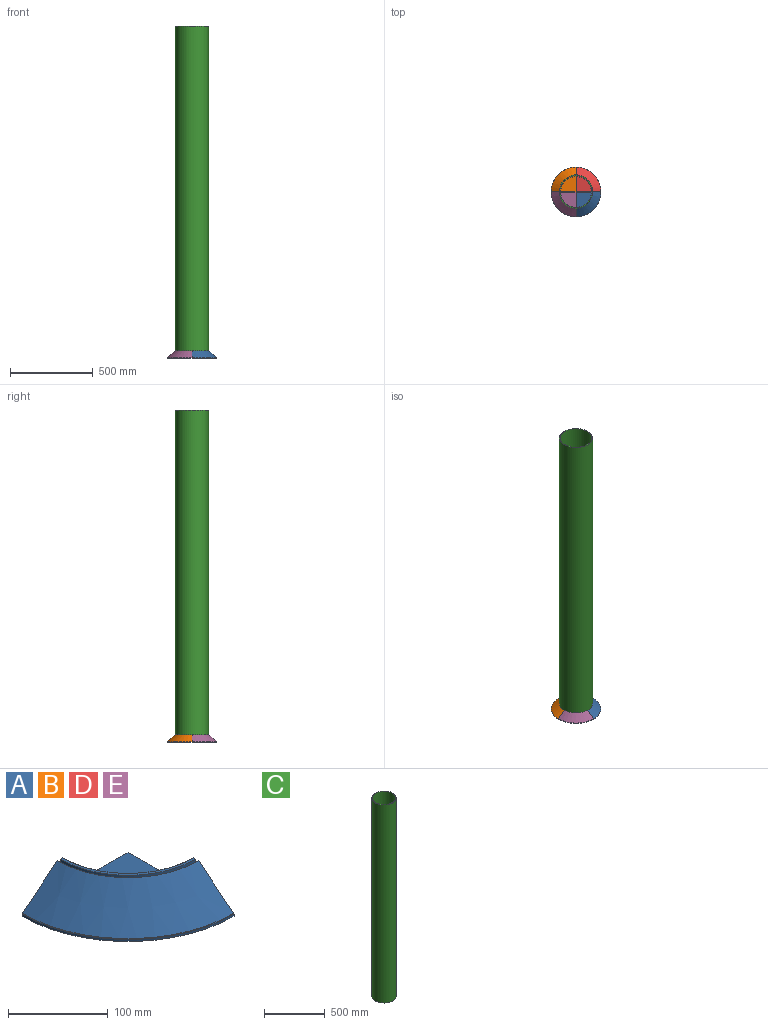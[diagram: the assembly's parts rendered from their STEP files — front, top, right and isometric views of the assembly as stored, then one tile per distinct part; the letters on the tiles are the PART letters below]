
ASSEMBLY  parts=5 mates=1
PART A: 13 faces, bbox 162.4x162.4x43 mm
  f0: plane 150x43mm, normal (1,0,0), area 1609.8mm2, adj f1,f2,f3,f4,f5,f6,f7,f8
  f1: plane 150x150mm, normal (0,0,-1), area 17671.5mm2, adj f0,f11,f12
  f2: plane 92x92mm, normal (0,0,1), area 6647.6mm2, adj f0,f6,f12
  f3: torus R=93mm, axis (0,0,1), area 227.9mm2, adj f0,f4,f6,f12
  f4: plane 96x96mm, normal (0,0,1), area 445.3mm2, adj f0,f3,f5,f12
  f5: cylinder r=96mm len=96mm, axis (0,0,-1), area 6031.9mm2, adj f0,f4,f7,f12
  f6: cylinder r=92mm len=92mm, axis (0,0,-1), area 5636mm2, adj f0,f2,f3,f12
  f7: plane 100x100mm, normal (0,0,1), area 615.8mm2, adj f0,f5,f10,f12
  f8: torus R=149mm, axis (0,0,1), area 210.9mm2, adj f0,f9,f11,f12
  f9: cone r=100mm half-angle=51.3deg, axis (0,0,-1), area 12459.4mm2, adj f0,f8,f10,f12
  f10: cylinder r=100mm len=100mm, axis (0,0,-1), area 6283.2mm2, adj f0,f7,f9,f12
  f11: cylinder r=150mm len=150mm, axis (0,0,1), area 593.6mm2, adj f0,f1,f8,f12
  f12: plane 150x43mm, normal (0,1,0), area 1609.8mm2, adj f0,f1,f2,f3,f4,f5,f6,f7
PART B: same geometry as A
PART C: 4 faces, bbox 200x200x2000 mm
  f0: cylinder r=96mm len=2000mm, axis (0,0,-1), area 1206371.6mm2, adj f2,f3
  f1: cylinder r=100mm len=2000mm, axis (0,0,-1), area 1256637.1mm2, adj f2,f3
  f2: plane 200x200mm, normal (0,0,1), area 2463mm2, adj f0,f1
  f3: plane 200x200mm, normal (0,0,-1), area 2463mm2, adj f0,f1
PART D: same geometry as A
PART E: same geometry as A
PLACE A rot(axis=(0,0,1),90deg) t=(0,0,0)mm
PLACE B rot(axis=(0,0,-1),90deg) t=(0,0,0)mm
PLACE C at identity
PLACE D rot(axis=(0,0,1),180deg) t=(0,0,0)mm
PLACE E at identity
MATE fastened E.f10 <-> C.f1  axis (0,0,1) through (0,0,0)mm
